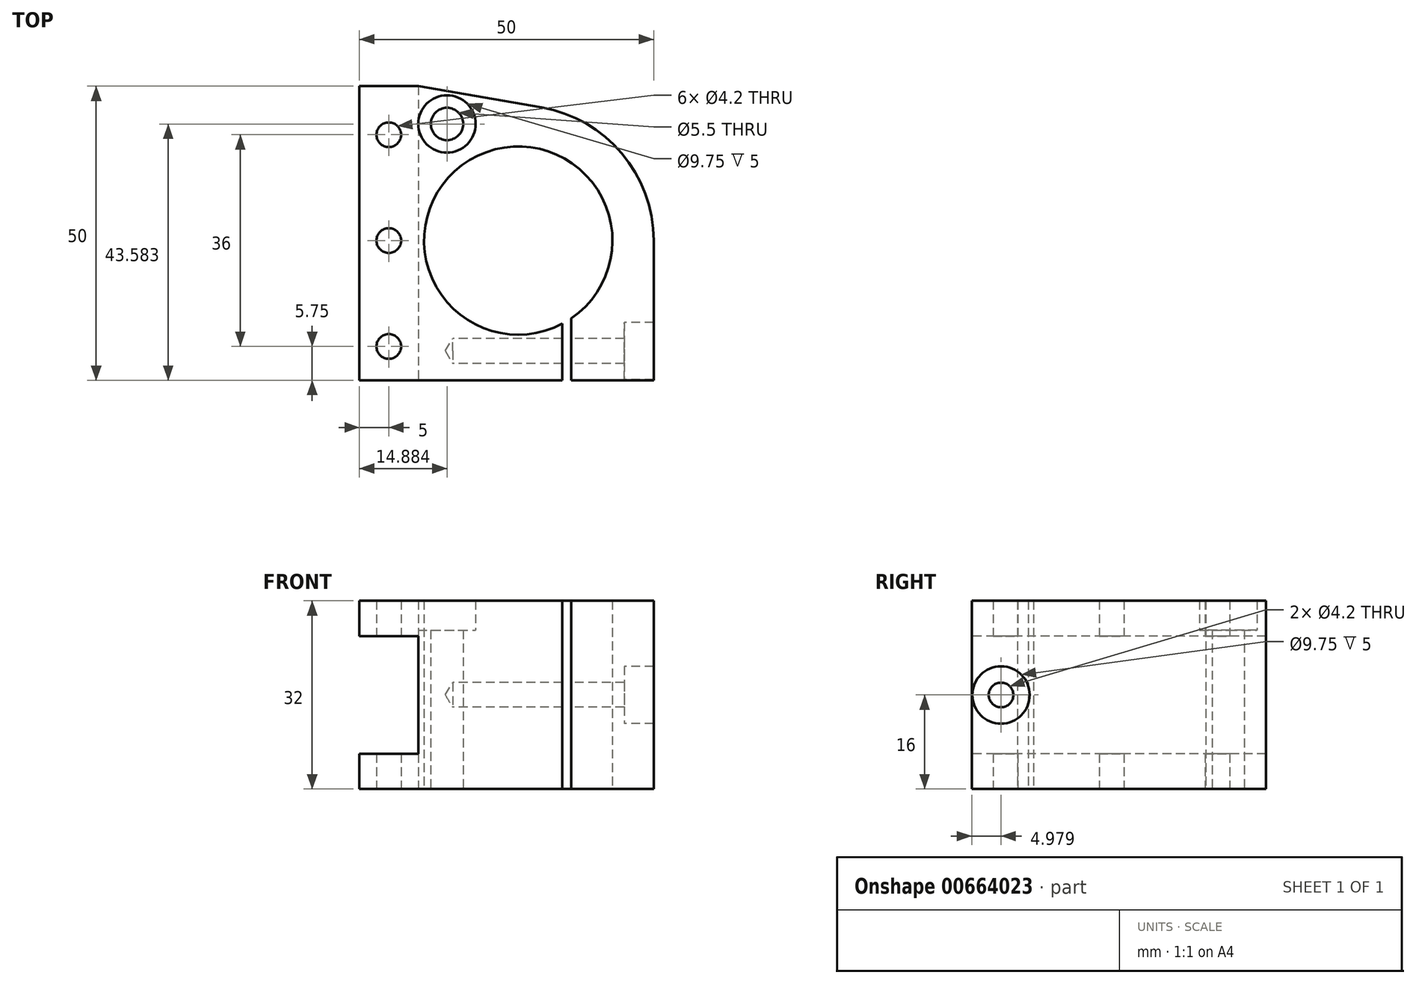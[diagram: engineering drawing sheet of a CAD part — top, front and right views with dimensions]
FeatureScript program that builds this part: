
annotation { "Feature Type Name" : "Feature", "Feature Type Description" : "" }
export const myFeature = defineFeature(function(context is Context, id is Id, definition is map)
    precondition{}
    {
        {
            var Q0;
            Q0=qCreatedBy(makeId("Top.planeOp"),FACE);
            var sketch = newSketch(context, id + "F0", { "sketchPlane" : qUnion([Q0])});
            skArc(sketch, "E0", {"start": v(9, -13.23) * mm, "mid": v(-8.26, 13.7) * mm, "end": v(7.5, -14.13) * mm});
            skLineSegment(sketch, "E1", {"start": v(23, 0) * mm, "end": v(23, -23.75) * mm});
            skLineSegment(sketch, "E2", {"start": v(23, -23.75) * mm, "end": v(9, -23.75) * mm});
            skLineSegment(sketch, "E3", {"start": v(-27, -23.75) * mm, "end": v(-27, 26.25) * mm});
            skLineSegment(sketch, "E4", {"start": v(-27, 26.25) * mm, "end": v(-17, 26.25) * mm});
            skLineSegment(sketch, "E5", {"start": v(-17, 26.25) * mm, "end": v(3.89, 22.67) * mm});
            skArc(sketch, "E6", {"start": v(23, 0) * mm, "mid": v(17.58, 14.83) * mm, "end": v(3.89, 22.67) * mm});
            skLineSegment(sketch, "E7", {"start": v(7.5, -23.75) * mm, "end": v(7.5, -14.13) * mm});
            skLineSegment(sketch, "E8", {"start": v(9, -23.75) * mm, "end": v(9, -13.23) * mm});
            skLineSegment(sketch, "E9.trimOffspring", {"start": v(7.5, -23.75) * mm, "end": v(-27, -23.75) * mm});
            skSolve(sketch);
        }
        {
            var Q0;
            Q0=makeQuery(id+"F0.imprint","IMPRINT",FACE,{"disambiguationData":[TD([[makeQuery(id+"F0.imprint","IMPRINT",EDGE,{"derivedFrom":sQuery(id+"F0.wireOp",EDGE,"E0")}),-1.0]])]});
            extrude(context, id + "F1", {"entities" : qUnion([Q0]), "depth" : 32 * mm, "offsetDistance" : 25.4 * mm});
        }
        {
            var Q0;
            Q0=makeQuery(id+"F1.opExtrude","SWEPT_FACE",FACE,{"disambiguationData":[OSD([sQuery(id+"F0.wireOp",EDGE,"E2")])]});
            var sketch = newSketch(context, id + "F2", { "sketchPlane" : qUnion([Q0])});
            skLineSegment(sketch, "E10.bottom", {"start": v(-27, 6) * mm, "end": v(-17, 6) * mm});
            skLineSegment(sketch, "E10.top", {"start": v(-27, 26) * mm, "end": v(-17, 26) * mm});
            skLineSegment(sketch, "E10.left", {"start": v(-27, 6) * mm, "end": v(-27, 26) * mm});
            skLineSegment(sketch, "E10.right", {"start": v(-17, 6) * mm, "end": v(-17, 26) * mm});
            skLineSegment(sketch, "E11", {"start": v(-17, 16) * mm, "end": v(23, 16) * mm, "construction": true});
            skSolve(sketch);
        }
        {
            var Q0;
            Q0 = qSketchRegion(id + "F2", true);
            extrude(context, id + "F3", {"entities" : qUnion([Q0]), "operationType" : NewBodyOperationType.REMOVE, "endBound" : BoundingType.THROUGH_ALL, "oppositeDirection" : true, "depth" : 25.4 * mm, "offsetDistance" : 25.4 * mm});
        }
        {
            var Q0;
            Q0=makeQuery(id+"F1.opExtrude","SWEPT_FACE",FACE,{"disambiguationData":[OSD([sQuery(id+"F0.wireOp",EDGE,"E1")])]});
            var sketch = newSketch(context, id + "F4", { "sketchPlane" : qUnion([Q0])});
            skPoint(sketch, "E12", {"position": v(-18.77, 16) * mm});
            skLineSegment(sketch, "E13", {"start": v(-18.77, 16) * mm, "end": v(-23.75, 16) * mm, "construction": true});
            skSolve(sketch);
        }
        {
            var Q0;
            Q0=sQuery(id+"F4.wireOp",VERTEX,"E12");
            var Q1;
            Q1=makeQuery(id+"F1.opExtrude","SWEPT_BODY",BODY,{"disambiguationData":[OSD([sQuery(id+"F0.wireOp",EDGE,"E0"),sQuery(id+"F0.wireOp",EDGE,"E1"),sQuery(id+"F0.wireOp",EDGE,"E2"),sQuery(id+"F0.wireOp",EDGE,"E3"),sQuery(id+"F0.wireOp",EDGE,"E4"),sQuery(id+"F0.wireOp",EDGE,"E5"),sQuery(id+"F0.wireOp",EDGE,"E6"),sQuery(id+"F0.wireOp",EDGE,"E7"),sQuery(id+"F0.wireOp",EDGE,"E8"),sQuery(id+"F0.wireOp",EDGE,"E9.trimOffspring")])]});
            hole(context, id + "F5", {"style" : HoleStyle.C_BORE, "endStyle" : HoleEndStyle.BLIND, "standardTappedOrClearance" : lookupTablePath({ "standard" : "ISO", "engagement" : "75%", "pitch" : "0.8 mm", "size" : "M5", "type" : "Tapped" }), "standardBlindInLast" : lookupTablePath({ "standard" : "ISO", "engagement" : "75%", "pitch" : "0.8 mm", "size" : "M5", "type" : "Tapped" }), "holeDiameter" : 4.2 * mm, "cBoreDiameter" : 9.75 * mm, "cBoreDepth" : 5 * mm, "majorDiameter" : 5 * mm, "showTappedDepth" : true, "holeDepth" : 34.15 * mm, "isTappedThrough" : true, "tappedDepth" : 31.75 * mm, "tapClearance" : 3, "locations" : qUnion([Q0]), "scope" : qUnion([Q1]), "startStyle" : HoleStartStyle.PART});
        }
        {
            var Q0;
            Q0=makeQuery(id+"F1.opExtrude","CAP_FACE",FACE,{"disambiguationData":[OSD([sQuery(id+"F0.wireOp",EDGE,"E0"),sQuery(id+"F0.wireOp",EDGE,"E1"),sQuery(id+"F0.wireOp",EDGE,"E2"),sQuery(id+"F0.wireOp",EDGE,"E3"),sQuery(id+"F0.wireOp",EDGE,"E4"),sQuery(id+"F0.wireOp",EDGE,"E5"),sQuery(id+"F0.wireOp",EDGE,"E6"),sQuery(id+"F0.wireOp",EDGE,"E7"),sQuery(id+"F0.wireOp",EDGE,"E8"),sQuery(id+"F0.wireOp",EDGE,"E9.trimOffspring")])],"isStart":false});
            var sketch = newSketch(context, id + "F6", { "sketchPlane" : qUnion([Q0])});
            skPoint(sketch, "E14", {"position": v(-22, 18) * mm});
            skPoint(sketch, "E15", {"position": v(-22, 0) * mm});
            skPoint(sketch, "E16", {"position": v(-22, -18) * mm});
            skLineSegment(sketch, "E17", {"start": v(-22, 18) * mm, "end": v(-22, 0) * mm, "construction": true});
            skLineSegment(sketch, "E18", {"start": v(-22, -18) * mm, "end": v(-22, 0) * mm, "construction": true});
            skSolve(sketch);
        }
        {
            var Q0;
            Q0=sQuery(id+"F6.wireOp",VERTEX,"E14");
            var Q1;
            Q1=sQuery(id+"F6.wireOp",VERTEX,"E15");
            var Q2;
            Q2=sQuery(id+"F6.wireOp",VERTEX,"E16");
            var Q3;
            Q3=makeQuery(id+"F1.opExtrude","SWEPT_BODY",BODY,{"disambiguationData":[OSD([sQuery(id+"F0.wireOp",EDGE,"E0"),sQuery(id+"F0.wireOp",EDGE,"E1"),sQuery(id+"F0.wireOp",EDGE,"E2"),sQuery(id+"F0.wireOp",EDGE,"E3"),sQuery(id+"F0.wireOp",EDGE,"E4"),sQuery(id+"F0.wireOp",EDGE,"E5"),sQuery(id+"F0.wireOp",EDGE,"E6"),sQuery(id+"F0.wireOp",EDGE,"E7"),sQuery(id+"F0.wireOp",EDGE,"E8"),sQuery(id+"F0.wireOp",EDGE,"E9.trimOffspring")])]});
            hole(context, id + "F7", {"style" : HoleStyle.SIMPLE, "endStyle" : HoleEndStyle.THROUGH, "standardTappedOrClearance" : lookupTablePath({ "standard" : "ISO", "engagement" : "75%", "pitch" : "0.8 mm", "size" : "M5", "type" : "Tapped" }), "standardBlindInLast" : lookupTablePath({ "standard" : "ISO", "engagement" : "75%", "pitch" : "0.8 mm", "size" : "M5", "type" : "Tapped" }), "holeDiameter" : 4.2 * mm, "majorDiameter" : 5 * mm, "showTappedDepth" : true, "isTappedThrough" : true, "tappedDepth" : 31.75 * mm, "tapClearance" : 3, "locations" : qUnion([Q0, Q1, Q2]), "scope" : qUnion([Q3]), "startStyle" : HoleStartStyle.PART});
        }
        {
            var Q0;
            Q0=makeQuery(id+"F1.opExtrude","CAP_FACE",FACE,{"disambiguationData":[OSD([sQuery(id+"F0.wireOp",EDGE,"E0"),sQuery(id+"F0.wireOp",EDGE,"E1"),sQuery(id+"F0.wireOp",EDGE,"E2"),sQuery(id+"F0.wireOp",EDGE,"E3"),sQuery(id+"F0.wireOp",EDGE,"E4"),sQuery(id+"F0.wireOp",EDGE,"E5"),sQuery(id+"F0.wireOp",EDGE,"E6"),sQuery(id+"F0.wireOp",EDGE,"E7"),sQuery(id+"F0.wireOp",EDGE,"E8"),sQuery(id+"F0.wireOp",EDGE,"E9.trimOffspring")])],"isStart":false});
            var sketch = newSketch(context, id + "F8", { "sketchPlane" : qUnion([Q0])});
            skPoint(sketch, "E19", {"position": v(-12.12, 19.83) * mm});
            skLineSegment(sketch, "E20", {"start": v(-12.12, 19.83) * mm, "end": v(0, 0) * mm, "construction": true});
            skSolve(sketch);
        }
        {
            var Q0;
            Q0=sQuery(id+"F8.wireOp",VERTEX,"E19");
            var Q1;
            Q1=makeQuery(id+"F1.opExtrude","SWEPT_BODY",BODY,{"disambiguationData":[OSD([sQuery(id+"F0.wireOp",EDGE,"E0"),sQuery(id+"F0.wireOp",EDGE,"E1"),sQuery(id+"F0.wireOp",EDGE,"E2"),sQuery(id+"F0.wireOp",EDGE,"E3"),sQuery(id+"F0.wireOp",EDGE,"E4"),sQuery(id+"F0.wireOp",EDGE,"E5"),sQuery(id+"F0.wireOp",EDGE,"E6"),sQuery(id+"F0.wireOp",EDGE,"E7"),sQuery(id+"F0.wireOp",EDGE,"E8"),sQuery(id+"F0.wireOp",EDGE,"E9.trimOffspring")])]});
            hole(context, id + "F9", {"style" : HoleStyle.C_BORE, "endStyle" : HoleEndStyle.THROUGH, "standardTappedOrClearance" : lookupTablePath({ "fit" : "Normal", "standard" : "ISO", "size" : "M5", "type" : "Clearance" }), "standardBlindInLast" : lookupTablePath({ "fit" : "Normal", "standard" : "ISO", "engagement" : "75%", "pitch" : "0.8 mm", "size" : "M5", "type" : "Clearance & tapped" }), "holeDiameter" : 5.5 * mm, "cBoreDiameter" : 9.75 * mm, "cBoreDepth" : 5 * mm, "majorDiameter" : 5 * mm, "isTappedThrough" : true, "tappedDepth" : 31.75 * mm, "tapClearance" : 3, "locations" : qUnion([Q0]), "scope" : qUnion([Q1]), "startStyle" : HoleStartStyle.PART});
        }
        {
            var Q0;
            Q0=makeQuery(id+"F1.opExtrude","CAP_FACE",FACE,{"disambiguationData":[OSD([sQuery(id+"F0.wireOp",EDGE,"E0"),sQuery(id+"F0.wireOp",EDGE,"E1"),sQuery(id+"F0.wireOp",EDGE,"E2"),sQuery(id+"F0.wireOp",EDGE,"E3"),sQuery(id+"F0.wireOp",EDGE,"E4"),sQuery(id+"F0.wireOp",EDGE,"E5"),sQuery(id+"F0.wireOp",EDGE,"E6"),sQuery(id+"F0.wireOp",EDGE,"E7"),sQuery(id+"F0.wireOp",EDGE,"E8"),sQuery(id+"F0.wireOp",EDGE,"E9.trimOffspring")])],"isStart":true});
            var sketch = newSketch(context, id + "F10", { "sketchPlane" : qUnion([Q0])});
            skCircle(sketch, "E21", {"center": v(-12.12, -19.83) * mm, "radius": 2.5 * mm});
            skSolve(sketch);
        }
        {
            var Q0;
            Q0 = qSketchRegion(id + "F10", true);
            extrude(context, id + "F11", {"entities" : qUnion([Q0]), "operationType" : NewBodyOperationType.REMOVE, "oppositeDirection" : true, "depth" : 7 * mm, "offsetDistance" : 25 * mm});
        }
    });
